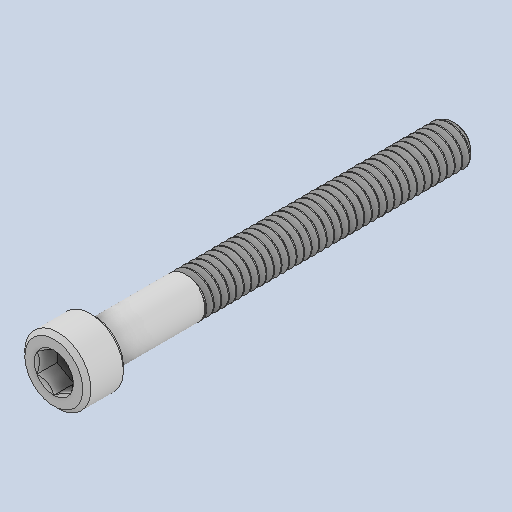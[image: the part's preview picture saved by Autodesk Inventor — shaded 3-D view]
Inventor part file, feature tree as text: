
AUTODESK INVENTOR PART (.ipt)
format: ipt  version: 2023 (Build 270158000, 158)  size: 703,488 bytes
history: native  units: in
note: dims shown in document units (in); Inventor stores cm internally (conversion verified against a paired STEP export)
features: revolve x1
ambient origin geometry x8: Origin, YZ Plane, XZ Plane, XY Plane, X Axis, Y Axis, Z Axis, Center Point
bodies: Solid1 (feature_tree)
feature tree (1):
  revolve  "Revolve2"  [1 undecoded]
note: 1 required parameter value undecoded (feature->parameter linkage not recoverable at this tier; creation-order binding heuristic only, values carry confidence <= 0.55)
